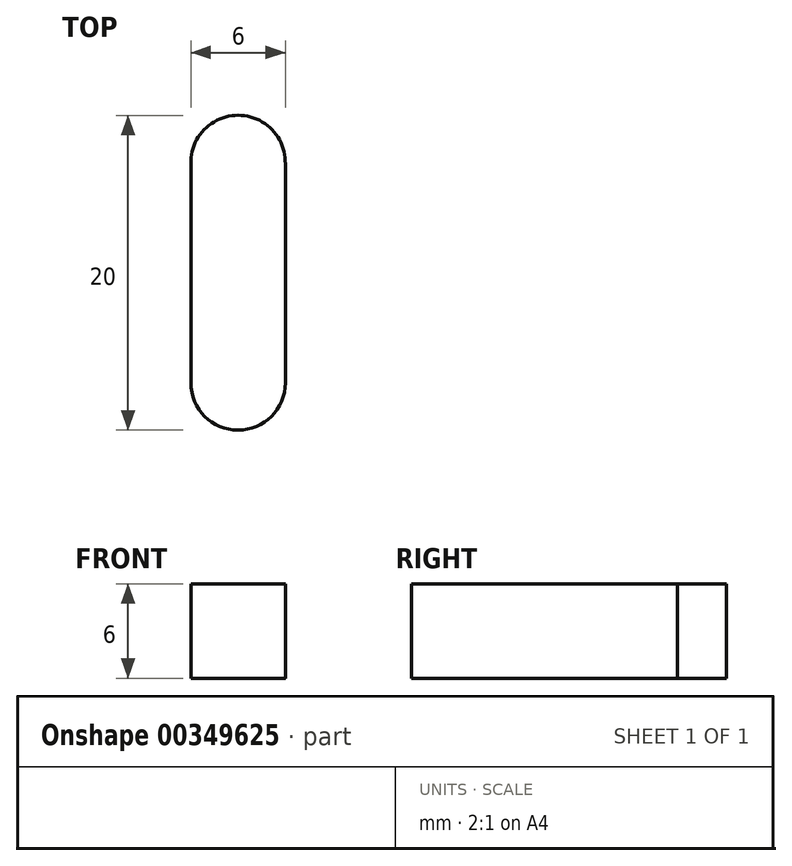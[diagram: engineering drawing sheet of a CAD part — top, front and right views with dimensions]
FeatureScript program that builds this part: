
annotation { "Feature Type Name" : "Feature", "Feature Type Description" : "" }
export const myFeature = defineFeature(function(context is Context, id is Id, definition is map)
    precondition{}
    {
        {
            var Q0;
            Q0=qCreatedBy(makeId("Top.planeOp"),FACE);
            var sketch = newSketch(context, id + "F0", { "sketchPlane" : qUnion([Q0])});
            skArc(sketch, "E0", {"start": v(2.86, 0) * mm, "mid": v(-0.13, 3.1) * mm, "end": v(-3.13, 0) * mm});
            skLineSegment(sketch, "E1", {"start": v(2.86, 0) * mm, "end": v(2.86, -13.9) * mm});
            skArc(sketch, "E2", {"start": v(-3.13, -13.9) * mm, "mid": v(-0.13, -16.9) * mm, "end": v(2.86, -13.9) * mm});
            skLineSegment(sketch, "E3", {"start": v(-3.13, 0) * mm, "end": v(-3.13, -13.9) * mm});
            skSolve(sketch);
        }
        {
            var Q0;
            Q0=makeQuery(id+"F0.imprint","IMPRINT",FACE,{"disambiguationData":[TD([[makeQuery(id+"F0.imprint","IMPRINT",EDGE,{"derivedFrom":sQuery(id+"F0.wireOp",EDGE,"E0")}),1.0]])]});
            extrude(context, id + "F1", {"entities" : qUnion([Q0]), "depth" : 6 * mm});
        }
    });
